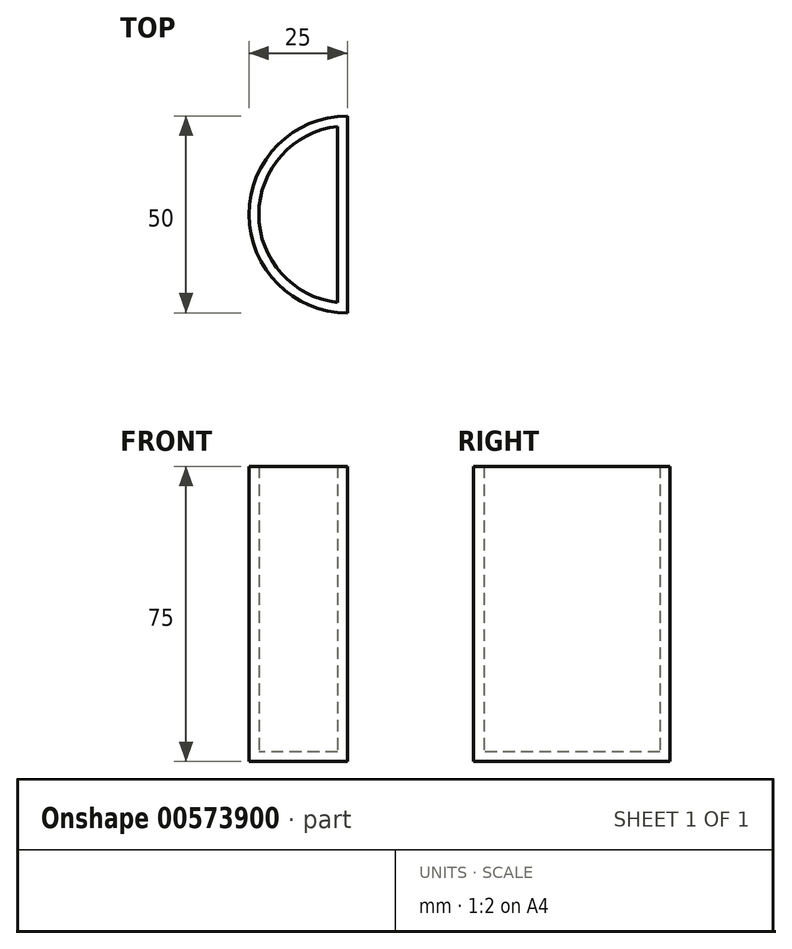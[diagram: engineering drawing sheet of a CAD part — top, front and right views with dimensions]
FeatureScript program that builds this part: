
annotation { "Feature Type Name" : "Feature", "Feature Type Description" : "" }
export const myFeature = defineFeature(function(context is Context, id is Id, definition is map)
    precondition{}
    {
        {
            var Q0;
            Q0=qCreatedBy(makeId("Top.planeOp"),FACE);
            var sketch = newSketch(context, id + "F0", { "sketchPlane" : qUnion([Q0])});
            skCircle(sketch, "E0", {"center": v(0, 0) * mm, "radius": 25 * mm});
            skLineSegment(sketch, "E1", {"start": v(0, 25) * mm, "end": v(0, -25) * mm});
            skSolve(sketch);
        }
        {
            var Q0;
            {var subQ0=sQuery(id+"F0.wireOp",EDGE,"E1");Q0=makeQuery(id+"F0.imprint","IMPRINT",FACE,{"disambiguationData":[TD([[makeQuery(id+"F0.imprint","IMPRINT",EDGE,{"derivedFrom":subQ0}),-1.0]])]});}
            extrude(context, id + "F1", {"entities" : qUnion([Q0]), "depth" : 75 * mm, "offsetDistance" : 25 * mm});
        }
        {
            var Q0;
            Q0=makeQuery(id+"F1.opExtrude","CAP_FACE",FACE,{"disambiguationData":[OSD([sQuery(id+"F0.wireOp",EDGE,"E0"),sQuery(id+"F0.wireOp",EDGE,"E1")])],"isStart":false});
            shell(context, id + "F2", {"entities" : qUnion([Q0]), "thickness" : 2.5 * mm});
        }
    });
